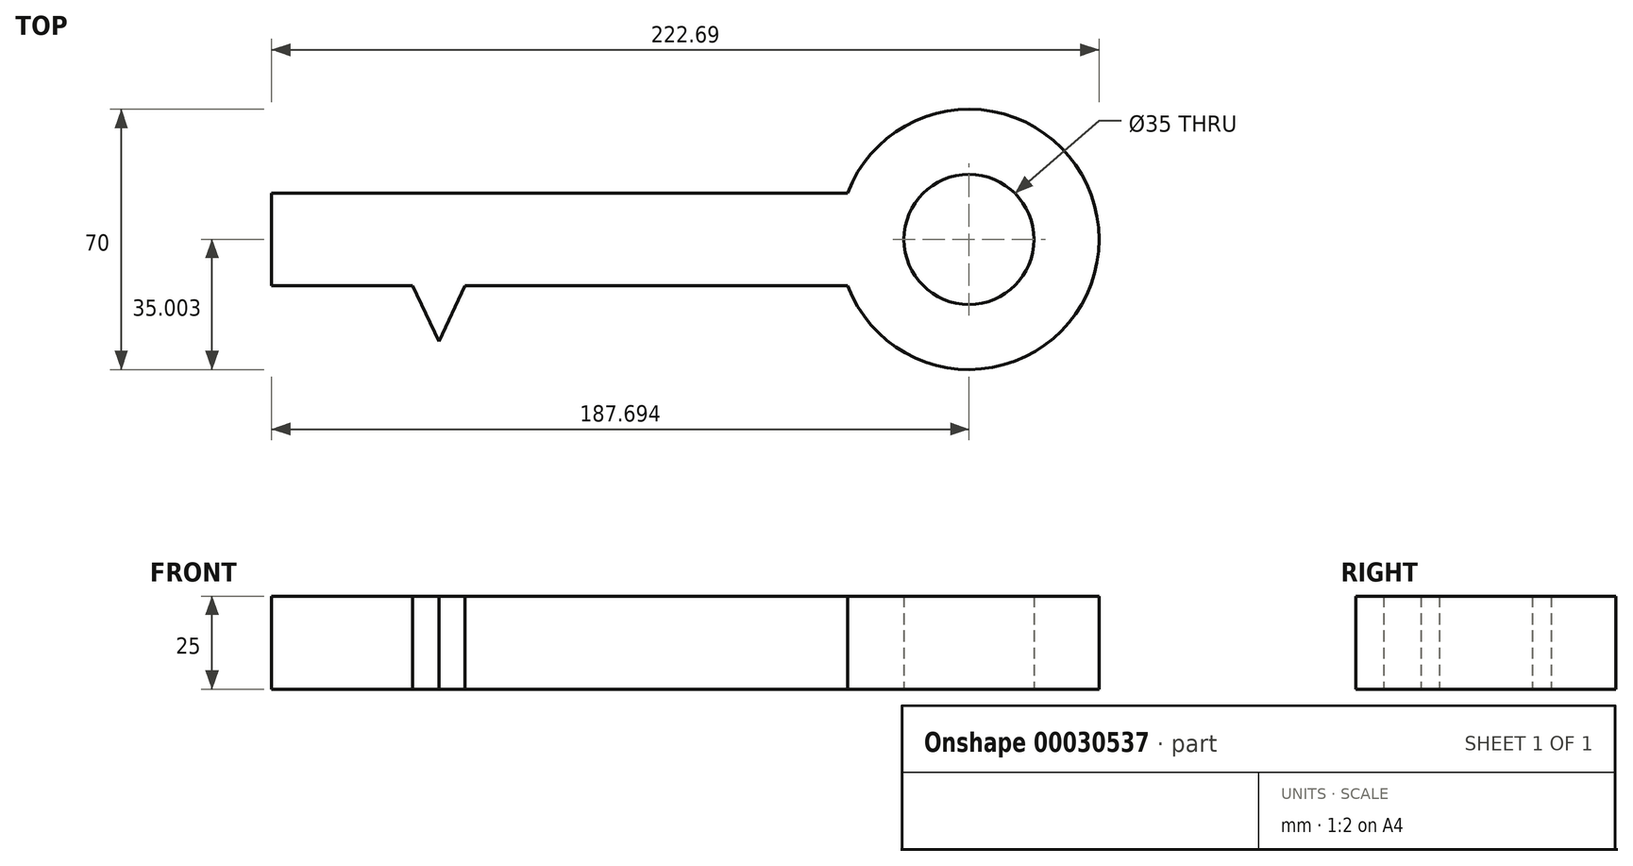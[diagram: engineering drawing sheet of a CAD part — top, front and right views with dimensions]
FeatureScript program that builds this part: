
annotation { "Feature Type Name" : "Feature", "Feature Type Description" : "" }
export const myFeature = defineFeature(function(context is Context, id is Id, definition is map)
    precondition{}
    {
        {
            var Q0;
            Q0=qCreatedBy(makeId("Top.planeOp"),FACE);
            var sketch = newSketch(context, id + "F0", { "sketchPlane" : qUnion([Q0])});
            skLineSegment(sketch, "E0.bottom", {"start": v(-125.97, 46.76) * mm, "end": v(29.03, 46.76) * mm});
            skLineSegment(sketch, "E0.top", {"start": v(-125.97, 21.76) * mm, "end": v(29.03, 21.76) * mm});
            skLineSegment(sketch, "E0.left", {"start": v(-125.97, 46.76) * mm, "end": v(-125.97, 21.76) * mm});
            skLineSegment(sketch, "E0.right", {"start": v(29.03, 46.76) * mm, "end": v(29.03, 21.76) * mm});
            skLineSegment(sketch, "E1.bottom", {"start": v(-125.97, 21.76) * mm, "end": v(-115.97, 21.76) * mm});
            skLineSegment(sketch, "E1.top", {"start": v(-125.97, -8.24) * mm, "end": v(-115.97, -8.24) * mm});
            skLineSegment(sketch, "E1.left", {"start": v(-125.97, 21.76) * mm, "end": v(-125.97, -8.24) * mm});
            skLineSegment(sketch, "E1.right", {"start": v(-115.97, 21.76) * mm, "end": v(-115.97, -8.24) * mm});
            skLineSegment(sketch, "E2.bottom", {"start": v(-105.97, 21.76) * mm, "end": v(-97.97, 21.76) * mm});
            skLineSegment(sketch, "E2.top", {"start": v(-105.97, 6.76) * mm, "end": v(-97.97, 6.76) * mm});
            skLineSegment(sketch, "E2.left", {"start": v(-105.97, 21.76) * mm, "end": v(-105.97, 6.76) * mm});
            skLineSegment(sketch, "E2.right", {"start": v(-97.97, 21.76) * mm, "end": v(-97.97, 6.76) * mm});
            skLineSegment(sketch, "E3", {"start": v(-87.97, 21.76) * mm, "end": v(-80.97, 6.76) * mm});
            skLineSegment(sketch, "E4", {"start": v(-73.97, 21.76) * mm, "end": v(-80.97, 6.76) * mm});
            skArc(sketch, "E5", {"start": v(29.03, 21.76) * mm, "mid": v(96.72, 34.26) * mm, "end": v(29.03, 46.76) * mm});
            skCircle(sketch, "E6", {"center": v(61.72, 34.26) * mm, "radius": 17.5 * mm});
            skLineSegment(sketch, "E7", {"start": v(-125.97, 34.26) * mm, "end": v(61.72, 34.26) * mm, "construction": true});
            skSolve(sketch);
        }
        {
            var Q0;
            Q0=makeQuery(id+"F0.imprint","IMPRINT",FACE,{"disambiguationData":[TD([[makeQuery(id+"F0.imprint","IMPRINT",EDGE,{"derivedFrom":sQuery(id+"F0.wireOp",EDGE,"E1.bottom")}),-1.0]])]});
            var Q1;
            Q1=makeQuery(id+"F0.imprint","IMPRINT",FACE,{"disambiguationData":[TD([[makeQuery(id+"F0.imprint","IMPRINT",EDGE,{"derivedFrom":sQuery(id+"F0.wireOp",EDGE,"E2.bottom")}),-1.0]])]});
            var Q2;
            {var subQ1=sQuery(id+"F0.wireOp",EDGE,"E3");Q2=makeQuery(id+"F0.imprint","IMPRINT",FACE,{"disambiguationData":[TD([[makeQuery(id+"F0.imprint","IMPRINT",EDGE,{"derivedFrom":subQ1}),1.0]])]});}
            var Q3;
            Q3=makeQuery(id+"F0.imprint","IMPRINT",FACE,{"disambiguationData":[TD([[makeQuery(id+"F0.imprint","IMPRINT",EDGE,{"derivedFrom":sQuery(id+"F0.wireOp",EDGE,"E0.bottom")}),-1.0]])]});
            var Q4;
            Q4=makeQuery(id+"F0.imprint","IMPRINT",FACE,{"disambiguationData":[TD([[makeQuery(id+"F0.imprint","IMPRINT",EDGE,{"derivedFrom":sQuery(id+"F0.wireOp",EDGE,"E0.right")}),1.0]])]});
            extrude(context, id + "F1", {"entities" : qUnion([Q0, Q1, Q2, Q3, Q4]), "depth" : 25 * mm});
        }
    });
